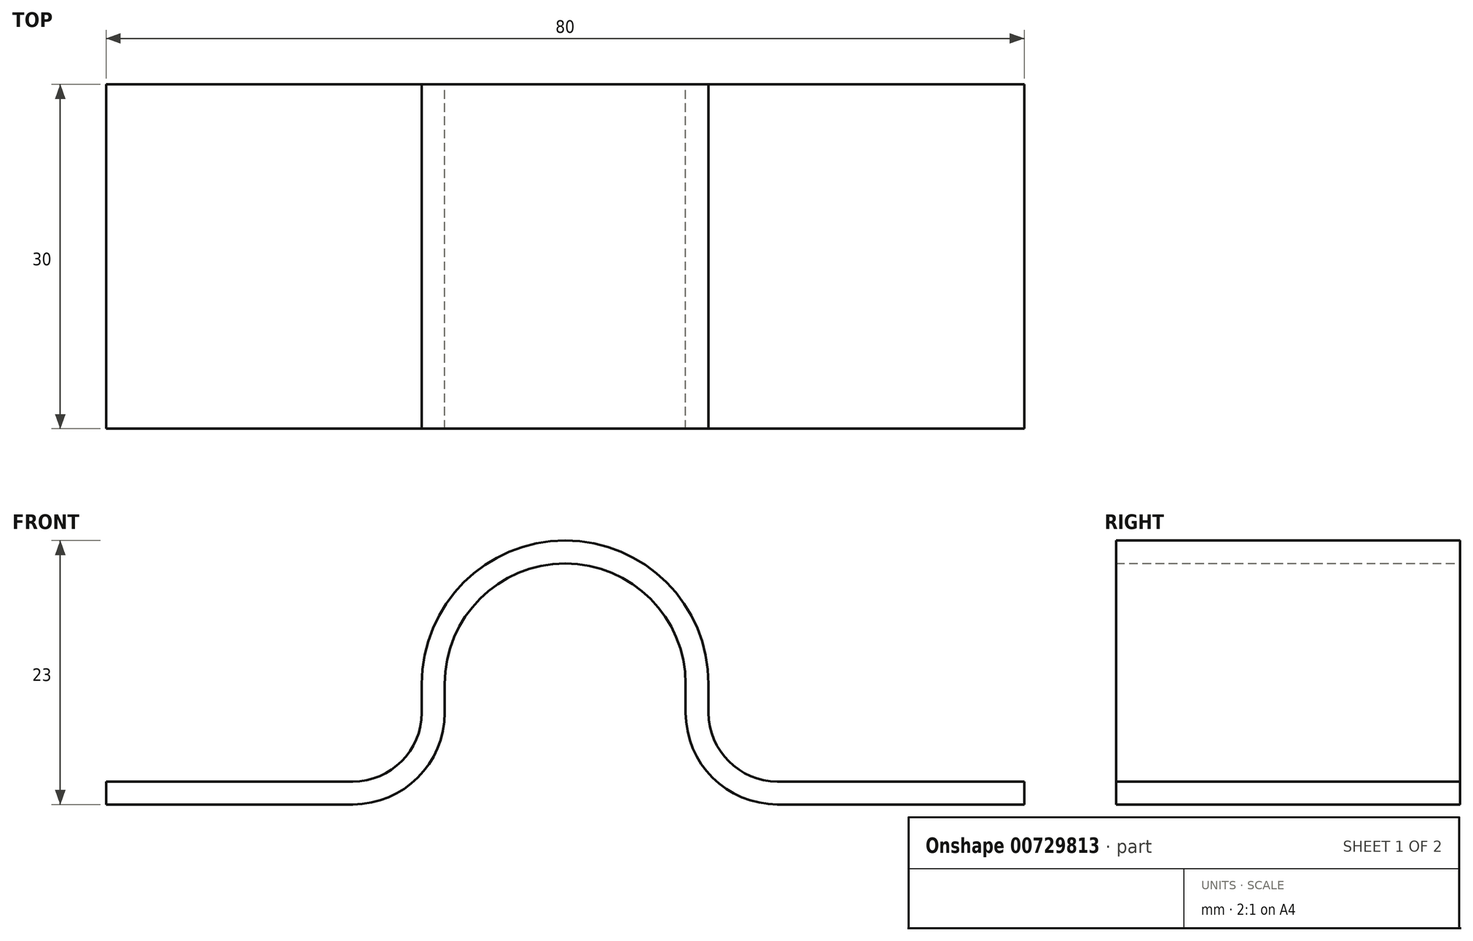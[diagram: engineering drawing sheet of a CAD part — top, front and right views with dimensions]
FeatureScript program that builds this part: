
annotation { "Feature Type Name" : "Feature", "Feature Type Description" : "" }
export const myFeature = defineFeature(function(context is Context, id is Id, definition is map)
    precondition{}
    {
        {
            var Q0;
            Q0=qCreatedBy(makeId("Front.planeOp"),FACE);
            var sketch = newSketch(context, id + "F0", { "sketchPlane" : qUnion([Q0])});
            skArc(sketch, "E0", {"start": v(10.5, 0) * mm, "mid": v(0, 10.5) * mm, "end": v(-10.5, 0) * mm});
            skLineSegment(sketch, "E1", {"start": v(-10.5, 0) * mm, "end": v(-10.5, -2.5) * mm});
            skLineSegment(sketch, "E2", {"start": v(-18.5, -10.5) * mm, "end": v(-40, -10.5) * mm});
            skLineSegment(sketch, "E3", {"start": v(10.5, 0) * mm, "end": v(10.5, -2.5) * mm});
            skLineSegment(sketch, "E4", {"start": v(18.5, -10.5) * mm, "end": v(40, -10.5) * mm});
            skLineSegment(sketch, "E5", {"start": v(-10.5, -10.5) * mm, "end": v(10.5, -10.5) * mm, "construction": true});
            skPoint(sketch, "E6.visualSharp", {"position": v(-10.5, -10.5) * mm});
            skArc(sketch, "E6.filletArc", {"start": v(-18.5, -10.5) * mm, "mid": v(-12.84, -8.16) * mm, "end": v(-10.5, -2.5) * mm});
            skPoint(sketch, "E7.visualSharp", {"position": v(10.5, -10.5) * mm});
            skArc(sketch, "E7.filletArc", {"start": v(10.5, -2.5) * mm, "mid": v(12.84, -8.16) * mm, "end": v(18.5, -10.5) * mm});
            skLineSegment(sketch, "E8.0", {"start": v(-18.5, -8.5) * mm, "end": v(-40, -8.5) * mm});
            skLineSegment(sketch, "E9.0", {"start": v(18.5, -8.5) * mm, "end": v(40, -8.5) * mm});
            skArc(sketch, "E9.1", {"start": v(12.5, -2.5) * mm, "mid": v(14.26, -6.74) * mm, "end": v(18.5, -8.5) * mm});
            skLineSegment(sketch, "E9.2", {"start": v(12.5, 0) * mm, "end": v(12.5, -2.5) * mm});
            skArc(sketch, "E9.4", {"start": v(-18.5, -8.5) * mm, "mid": v(-14.26, -6.74) * mm, "end": v(-12.5, -2.5) * mm});
            skLineSegment(sketch, "E9.5", {"start": v(-12.5, 0) * mm, "end": v(-12.5, -2.5) * mm});
            skArc(sketch, "E9.6", {"start": v(12.5, 0) * mm, "mid": v(0, 12.5) * mm, "end": v(-12.5, 0) * mm});
            skLineSegment(sketch, "E10", {"start": v(-40, -10.5) * mm, "end": v(-40, -8.5) * mm});
            skLineSegment(sketch, "E11", {"start": v(40, -10.5) * mm, "end": v(40, -8.5) * mm});
            skSolve(sketch);
        }
        {
            var Q0;
            Q0 = qSketchRegion(id + "F0", true);
            extrude(context, id + "F1", {"entities" : qUnion([Q0]), "depth" : 30 * mm, "offsetDistance" : 25 * mm});
        }
    });
